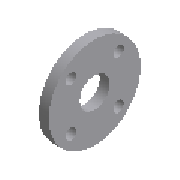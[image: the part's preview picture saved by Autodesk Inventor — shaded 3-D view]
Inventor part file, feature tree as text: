
AUTODESK INVENTOR PART (.ipt)
format: ipt  version: 2024.2 (Build 282272000, 272)  size: 169,984 bytes
history: native  units: mm (DEFAULTED — no unit token found)
features: other x5, revolve x1, extrude x1, pattern_circular x1
ambient origin geometry x8: Origin, YZ Plane, XZ Plane, XY Plane, X Axis, Y Axis, Z Axis, Center Point
bodies: Solid1 (feature_tree)
feature tree (8):
  revolve  "Revolution1"  Angle=90.0deg
  extrude  "Extrusion1"  Depth=200.0mm
  pattern_circular  "Circular Pattern1"  [2 undecoded]
  other  "Work Axis1"
  other  "Work Point1"
  other  "Work Axis2"
  other  "Work Point2"
  other  "Work Point3"
note: 2 required parameter values undecoded (feature->parameter linkage not recoverable at this tier; creation-order binding heuristic only, values carry confidence <= 0.55)
